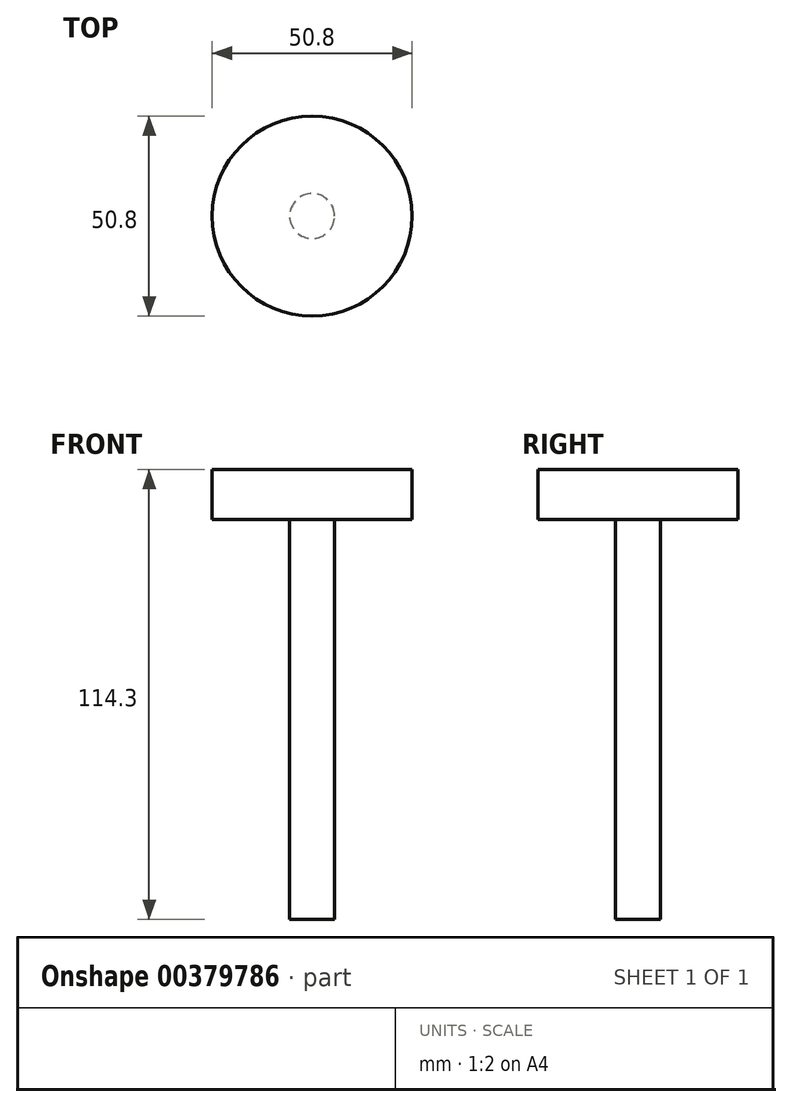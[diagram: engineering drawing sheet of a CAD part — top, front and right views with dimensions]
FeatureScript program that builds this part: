
annotation { "Feature Type Name" : "Feature", "Feature Type Description" : "" }
export const myFeature = defineFeature(function(context is Context, id is Id, definition is map)
    precondition{}
    {
        {
            var Q0;
            Q0=qCreatedBy(makeId("Top.planeOp"),FACE);
            cPlane(context, id + "F0", {"entities" : qUnion([Q0]), "cplaneType" : CPlaneType.OFFSET, "offset" : 50.8 * mm, "width" : 152.4 * mm, "height" : 152.4 * mm});
        }
        {
            var Q0;
            Q0=qCreatedBy(id+"F0.planeOp",FACE);
            var sketch = newSketch(context, id + "F1", { "sketchPlane" : qUnion([Q0])});
            skCircle(sketch, "E0", {"center": v(0, 0) * mm, "radius": 5.72 * mm});
            skSolve(sketch);
        }
        {
            var Q0;
            Q0 = qSketchRegion(id + "F1", true);
            extrude(context, id + "F2", {"entities" : qUnion([Q0]), "oppositeDirection" : true, "depth" : 101.6 * mm});
        }
        {
            var Q0;
            Q0=qCreatedBy(id+"F0.planeOp",FACE);
            var sketch = newSketch(context, id + "F3", { "sketchPlane" : qUnion([Q0])});
            skCircle(sketch, "E1", {"center": v(0, 0) * mm, "radius": 25.4 * mm});
            skSolve(sketch);
        }
        {
            var Q0;
            Q0 = qSketchRegion(id + "F3", true);
            extrude(context, id + "F4", {"entities" : qUnion([Q0]), "operationType" : NewBodyOperationType.ADD, "depth" : 12.7 * mm});
        }
    });
